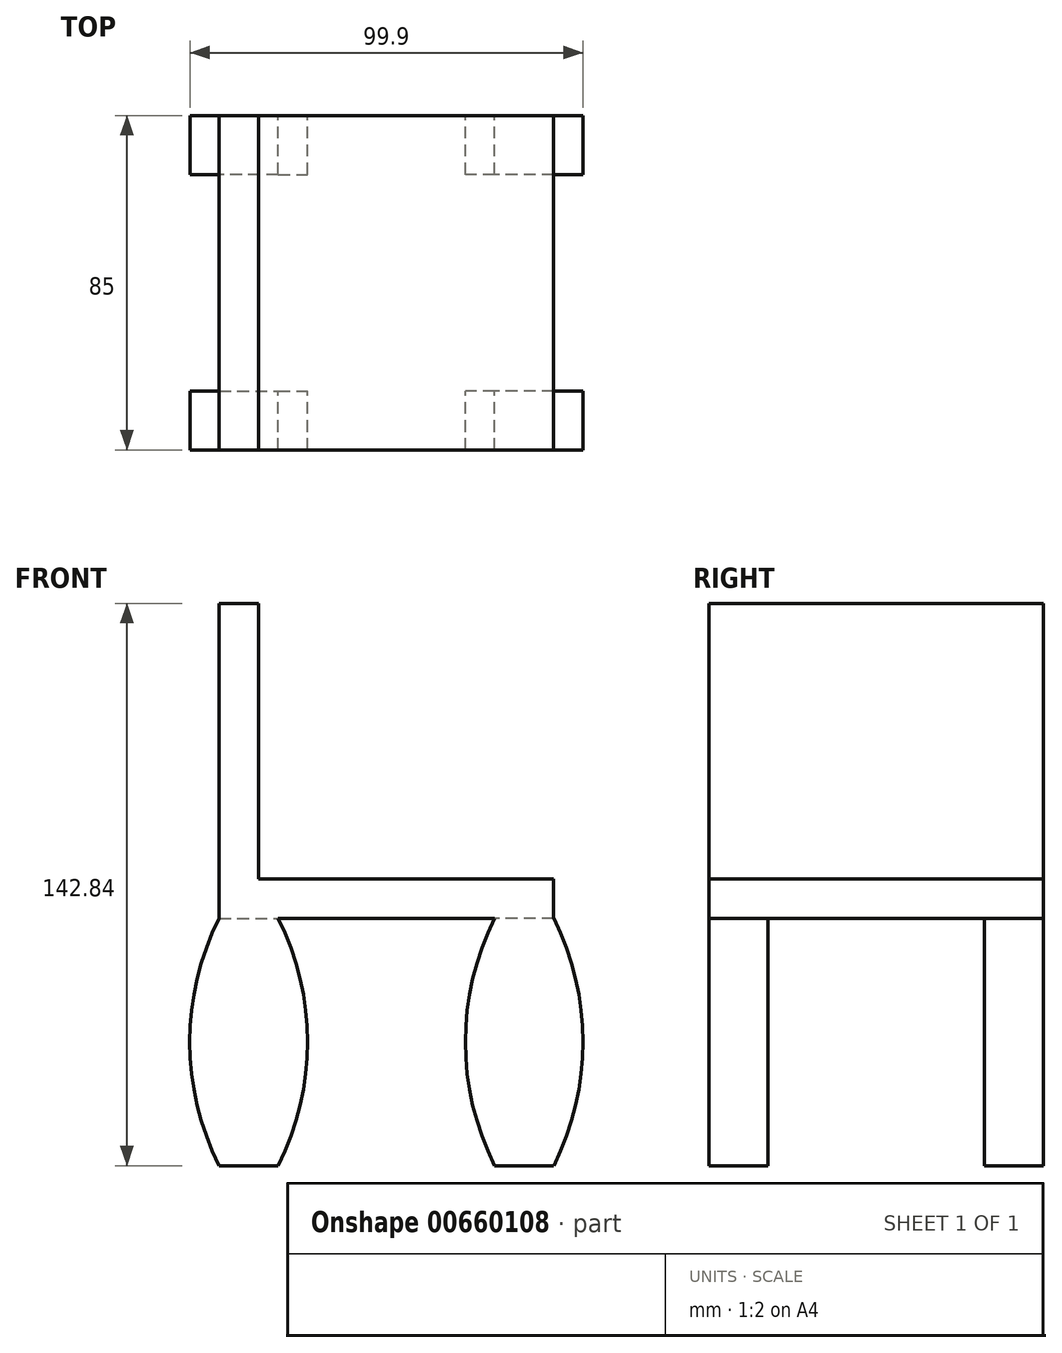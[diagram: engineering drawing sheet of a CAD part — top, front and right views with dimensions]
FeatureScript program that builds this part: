
annotation { "Feature Type Name" : "Feature", "Feature Type Description" : "" }
export const myFeature = defineFeature(function(context is Context, id is Id, definition is map)
    precondition{}
    {
        {
            var Q0;
            Q0=qCreatedBy(makeId("Front.planeOp"),FACE);
            var sketch = newSketch(context, id + "F0", { "sketchPlane" : qUnion([Q0])});
            skLineSegment(sketch, "E0", {"start": v(-27.53, -47.91) * mm, "end": v(-12.53, -47.91) * mm});
            skArc(sketch, "E1", {"start": v(-27.53, 14.93) * mm, "mid": v(-34.98, -16.49) * mm, "end": v(-27.53, -47.91) * mm});
            skArc(sketch, "E2", {"start": v(-12.53, -47.91) * mm, "mid": v(-5.08, -16.49) * mm, "end": v(-12.53, 14.93) * mm});
            skLineSegment(sketch, "E3", {"start": v(-12.53, 14.93) * mm, "end": v(-27.53, 14.93) * mm});
            skSolve(sketch);
        }
        {
            var Q0;
            Q0=makeQuery(id+"F0.imprint","IMPRINT",FACE,{"disambiguationData":[TD([[makeQuery(id+"F0.imprint","IMPRINT",EDGE,{"derivedFrom":sQuery(id+"F0.wireOp",EDGE,"E0")}),1.0]])]});
            extrude(context, id + "F1", {"entities" : qUnion([Q0]), "endBound" : BoundingType.SYMMETRIC, "depth" : 15 * mm, "offsetDistance" : 25 * mm});
        }
        {
            var Q0;
            Q0=makeQuery(id+"F1.opExtrude","SWEPT_BODY",BODY,{"disambiguationData":[OSD([sQuery(id+"F0.wireOp",EDGE,"E0"),sQuery(id+"F0.wireOp",EDGE,"E1"),sQuery(id+"F0.wireOp",EDGE,"E2"),sQuery(id+"F0.wireOp",EDGE,"E3")])]});
            transform(context, id + "F2", {"entities" : qUnion([Q0]), "transformType" : TransformType.TRANSLATION_3D, "dx" : 70 * mm, "dy" : 0 * mm, "dz" : 0 * mm, "makeCopy" : true});
        }
        {
            var Q0;
            Q0=makeQuery(id+"F1.opExtrude","SWEPT_BODY",BODY,{"disambiguationData":[OSD([sQuery(id+"F0.wireOp",EDGE,"E0"),sQuery(id+"F0.wireOp",EDGE,"E1"),sQuery(id+"F0.wireOp",EDGE,"E2"),sQuery(id+"F0.wireOp",EDGE,"E3")])]});
            transform(context, id + "F3", {"entities" : qUnion([Q0]), "transformType" : TransformType.TRANSLATION_3D, "dx" : 0 * mm, "dy" : 70 * mm, "dz" : 0 * mm, "makeCopy" : true});
        }
        {
            var Q0;
            Q0=makeQuery(id+"F2.opPattern","COPY",BODY,{"derivedFrom":makeQuery(id+"F1.opExtrude","SWEPT_BODY",BODY,{"disambiguationData":[OSD([sQuery(id+"F0.wireOp",EDGE,"E0"),sQuery(id+"F0.wireOp",EDGE,"E1"),sQuery(id+"F0.wireOp",EDGE,"E2"),sQuery(id+"F0.wireOp",EDGE,"E3")])]}),"instanceName":"1"});
            transform(context, id + "F4", {"entities" : qUnion([Q0]), "transformType" : TransformType.TRANSLATION_3D, "dx" : 0 * mm, "dy" : 70 * mm, "dz" : 0 * mm, "makeCopy" : true});
        }
        {
            var Q0;
            Q0=makeQuery(id+"F1.opExtrude","SWEPT_FACE",FACE,{"disambiguationData":[OSD([sQuery(id+"F0.wireOp",EDGE,"E3")])]});
            extrude(context, id + "F5", {"entities" : qUnion([Q0]), "operationType" : NewBodyOperationType.ADD, "depth" : 10 * mm, "offsetDistance" : 25 * mm});
        }
        {
            var Q0;
            Q0=makeQuery(id+"F5.opExtrude","SWEPT_FACE",FACE,{"disambiguationData":[OSD([sQuery(id+"F0.wireOp",EDGE,"E2"),sQuery(id+"F0.wireOp",EDGE,"E3")])]});
            extrude(context, id + "F6", {"entities" : qUnion([Q0]), "operationType" : NewBodyOperationType.ADD, "depth" : 70 * mm, "offsetDistance" : 25 * mm});
        }
        {
            var Q0;
            {var subQ0=sQuery(id+"F0.wireOp",EDGE,"E3");var subQ1=sQuery(id+"F0.wireOp",EDGE,"E2");var subQ2=makeQuery(id+"F1.opExtrude","CAP_FACE",FACE,{"disambiguationData":[OSD([sQuery(id+"F0.wireOp",EDGE,"E0"),sQuery(id+"F0.wireOp",EDGE,"E1"),subQ1,subQ0])],"isStart":true});Q0=makeQuery(id+"F6.boolean.opBoolean","MERGE",FACE,{"derivedFrom":[makeQuery(id+"F2.opPattern","COPY",FACE,{"derivedFrom":subQ2,"instanceName":"1"}),makeQuery(id+"F5.boolean.opBoolean","MERGE",FACE,{"derivedFrom":[subQ2,makeQuery(id+"F5.opExtrude","SWEPT_FACE",FACE,{"disambiguationData":[OSD([subQ0]),TDD([makeQuery(id+"F1.opExtrude","CAP_EDGE",EDGE,{"disambiguationData":[OSD([subQ0])],"isStart":true})])]})]}),makeQuery(id+"F6.opExtrude","SWEPT_FACE",FACE,{"disambiguationData":[OSD([subQ1,subQ0]),TDD([makeQuery(id+"F5.opExtrude","SWEPT_EDGE",EDGE,{"disambiguationData":[OSD([subQ1,subQ0]),TDD([makeQuery(id+"F1.opExtrude","CAP_VERTEX",VERTEX,{"disambiguationData":[OSD([subQ1,subQ0])],"isStart":true})])]})])]})]});}
            var sketch = newSketch(context, id + "F7", { "sketchPlane" : qUnion([Q0])});
            skLineSegment(sketch, "E4", {"start": v(-57.47, 14.93) * mm, "end": v(-42.47, 14.93) * mm});
            skLineSegment(sketch, "E5", {"start": v(-42.47, 14.93) * mm, "end": v(-42.47, 24.93) * mm});
            skLineSegment(sketch, "E6", {"start": v(-42.47, 24.93) * mm, "end": v(-57.47, 24.93) * mm});
            skLineSegment(sketch, "E7", {"start": v(-57.47, 24.93) * mm, "end": v(-57.47, 14.93) * mm});
            skSolve(sketch);
        }
        {
            var Q0;
            Q0=makeQuery(id+"F7.imprint","IMPRINT",FACE,{"disambiguationData":[TD([[makeQuery(id+"F7.imprint","IMPRINT",EDGE,{"derivedFrom":sQuery(id+"F7.wireOp",EDGE,"E4")}),1.0]])]});
            extrude(context, id + "F8", {"entities" : qUnion([Q0]), "operationType" : NewBodyOperationType.ADD, "depth" : 70 * mm, "offsetDistance" : 25 * mm});
        }
        {
            var Q0;
            Q0=makeQuery(id+"F8.opExtrude","SWEPT_FACE",FACE,{"disambiguationData":[OSD([sQuery(id+"F7.wireOp",EDGE,"E5")])]});
            extrude(context, id + "F9", {"entities" : qUnion([Q0]), "operationType" : NewBodyOperationType.ADD, "depth" : 70 * mm, "offsetDistance" : 25 * mm});
        }
        {
            var Q0;
            {var subQ0=sQuery(id+"F7.wireOp",EDGE,"E6");var subQ1=sQuery(id+"F0.wireOp",EDGE,"E3");var subQ2=sQuery(id+"F0.wireOp",EDGE,"E2");Q0=makeQuery(id+"F9.boolean.opBoolean","MERGE",FACE,{"derivedFrom":[makeQuery(id+"F8.boolean.opBoolean","MERGE",FACE,{"derivedFrom":[makeQuery(id+"F6.boolean.opBoolean","MERGE",FACE,{"derivedFrom":[makeQuery(id+"F5.opExtrude","CAP_FACE",FACE,{"disambiguationData":[OSD([subQ1])],"isStart":false}),makeQuery(id+"F6.opExtrude","SWEPT_FACE",FACE,{"disambiguationData":[OSD([subQ2,subQ1]),TDD([makeQuery(id+"F5.opExtrude","CAP_EDGE",EDGE,{"disambiguationData":[OSD([subQ2,subQ1])],"isStart":false})])]})]}),makeQuery(id+"F8.opExtrude","SWEPT_FACE",FACE,{"disambiguationData":[OSD([subQ0])]})]}),makeQuery(id+"F9.opExtrude","SWEPT_FACE",FACE,{"disambiguationData":[OSD([subQ2,subQ1,sQuery(id+"F7.wireOp",EDGE,"E5"),subQ0])]})]});}
            var sketch = newSketch(context, id + "F10", { "sketchPlane" : qUnion([Q0])});
            skLineSegment(sketch, "E8.bottom", {"start": v(-27.53, 77.5) * mm, "end": v(-17.53, 77.5) * mm});
            skLineSegment(sketch, "E8.top", {"start": v(-27.53, -7.5) * mm, "end": v(-17.53, -7.5) * mm});
            skLineSegment(sketch, "E8.left", {"start": v(-27.53, 77.5) * mm, "end": v(-27.53, -7.5) * mm});
            skLineSegment(sketch, "E8.right", {"start": v(-17.53, 77.5) * mm, "end": v(-17.53, -7.5) * mm});
            skSolve(sketch);
        }
        {
            var Q0;
            Q0=makeQuery(id+"F10.imprint","IMPRINT",FACE,{"disambiguationData":[TD([[makeQuery(id+"F10.imprint","IMPRINT",EDGE,{"derivedFrom":sQuery(id+"F10.wireOp",EDGE,"E8.bottom")}),1.0]])]});
            extrude(context, id + "F11", {"entities" : qUnion([Q0]), "operationType" : NewBodyOperationType.ADD, "depth" : 70 * mm, "offsetDistance" : 25 * mm});
        }
    });
